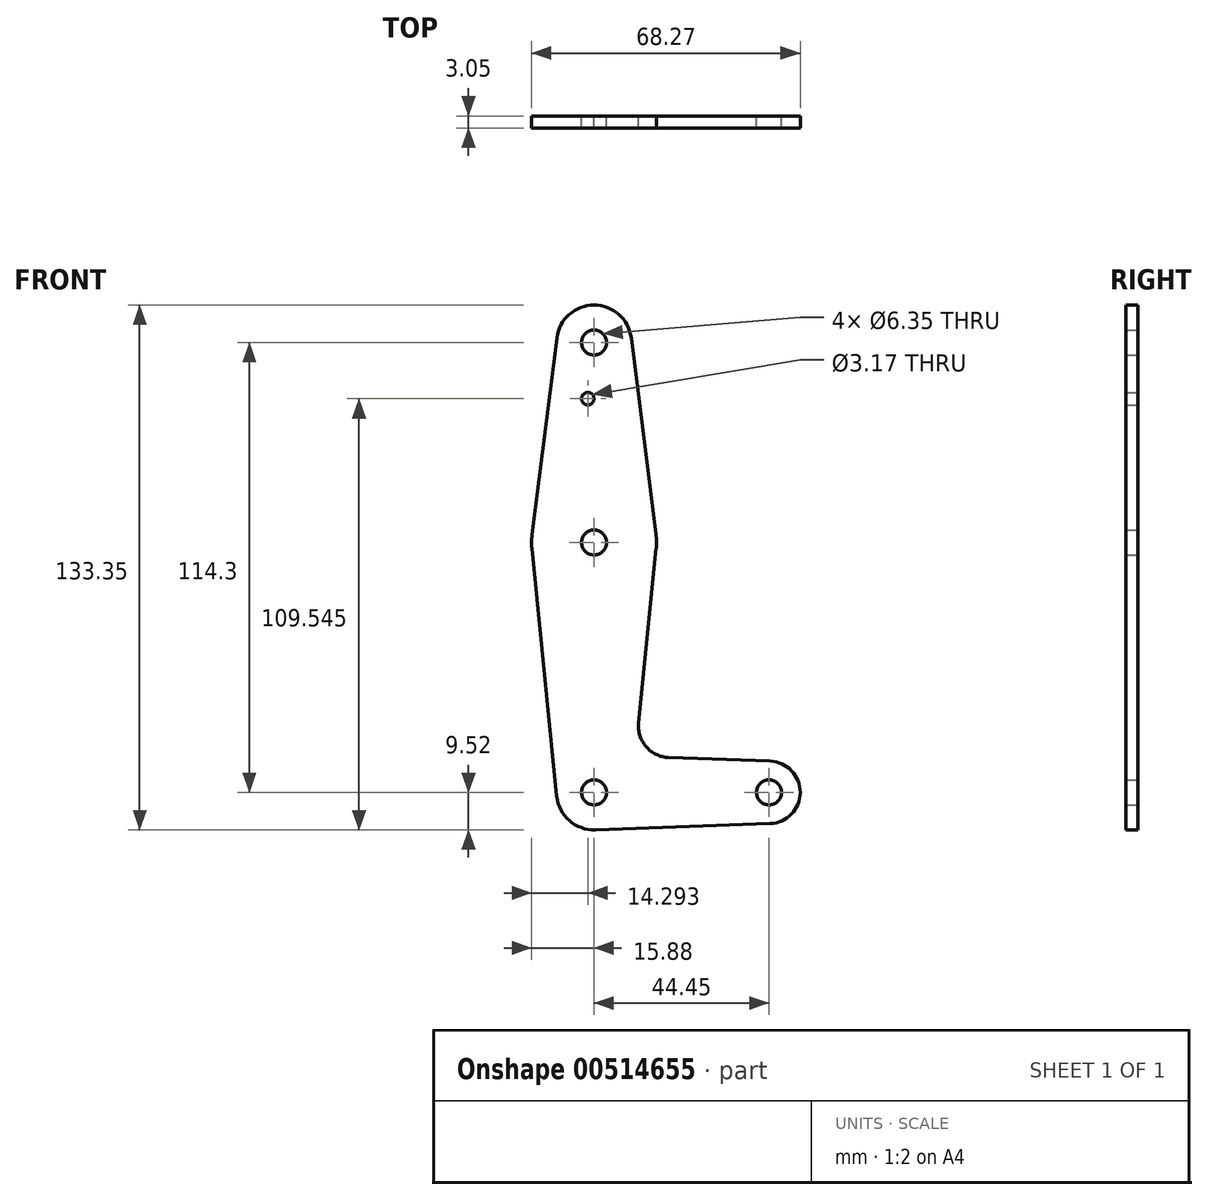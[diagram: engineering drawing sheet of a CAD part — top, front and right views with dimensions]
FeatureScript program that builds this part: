
annotation { "Feature Type Name" : "Feature", "Feature Type Description" : "" }
export const myFeature = defineFeature(function(context is Context, id is Id, definition is map)
    precondition{}
    {
        {
            var Q0;
            Q0=qCreatedBy(makeId("Front.planeOp"),FACE);
            var sketch = newSketch(context, id + "F0", { "sketchPlane" : qUnion([Q0])});
            skLineSegment(sketch, "E0", {"start": v(0, 114.3) * mm, "end": v(0, 0) * mm, "construction": true});
            skLineSegment(sketch, "E1", {"start": v(0, 0) * mm, "end": v(44.45, 0) * mm, "construction": true});
            skCircle(sketch, "E2", {"center": v(0, 114.3) * mm, "radius": 9.53 * mm});
            skCircle(sketch, "E3", {"center": v(0, 63.5) * mm, "radius": 15.88 * mm});
            skCircle(sketch, "E4", {"center": v(0, 0) * mm, "radius": 9.53 * mm});
            skCircle(sketch, "E5", {"center": v(44.45, 0) * mm, "radius": 7.94 * mm});
            skLineSegment(sketch, "E6", {"start": v(-9.45, 115.5) * mm, "end": v(-15.75, 65.48) * mm});
            skLineSegment(sketch, "E7", {"start": v(-15.8, 61.91) * mm, "end": v(-9.48, -0.95) * mm});
            skPoint(sketch, "E7.startSnap0", {"position": v(0, 57.15) * mm});
            skLineSegment(sketch, "E8.MirrorCS", {"start": v(9.45, 115.5) * mm, "end": v(15.75, 65.48) * mm});
            skLineSegment(sketch, "E9.MirrorCS", {"start": v(15.8, 61.91) * mm, "end": v(11.34, 17.6) * mm});
            skLineSegment(sketch, "E10", {"start": v(18.97, 8.85) * mm, "end": v(44.73, 7.93) * mm});
            skLineSegment(sketch, "E11", {"start": v(0.34, -9.52) * mm, "end": v(44.73, -7.93) * mm});
            skCircle(sketch, "E12", {"center": v(-1.59, 100.03) * mm, "radius": 1.59 * mm});
            skPoint(sketch, "E13.newPointA", {"position": v(9.48, -0.95) * mm});
            skArc(sketch, "E13.filletArc", {"start": v(11.34, 17.6) * mm, "mid": v(13.26, 11.57) * mm, "end": v(18.97, 8.85) * mm});
            skCircle(sketch, "E14", {"center": v(0, 114.3) * mm, "radius": 3.18 * mm});
            skCircle(sketch, "E15", {"center": v(0, 63.5) * mm, "radius": 3.18 * mm});
            skCircle(sketch, "E16", {"center": v(0, 0) * mm, "radius": 3.18 * mm});
            skCircle(sketch, "E17", {"center": v(44.45, 0) * mm, "radius": 3.18 * mm});
            skSolve(sketch);
        }
        {
            var Q0;
            Q0 = qSketchRegion(id + "F0", true);
            extrude(context, id + "F1", {"entities" : qUnion([Q0]), "depth" : 3.05 * mm, "offsetDistance" : 25.4 * mm});
        }
    });
